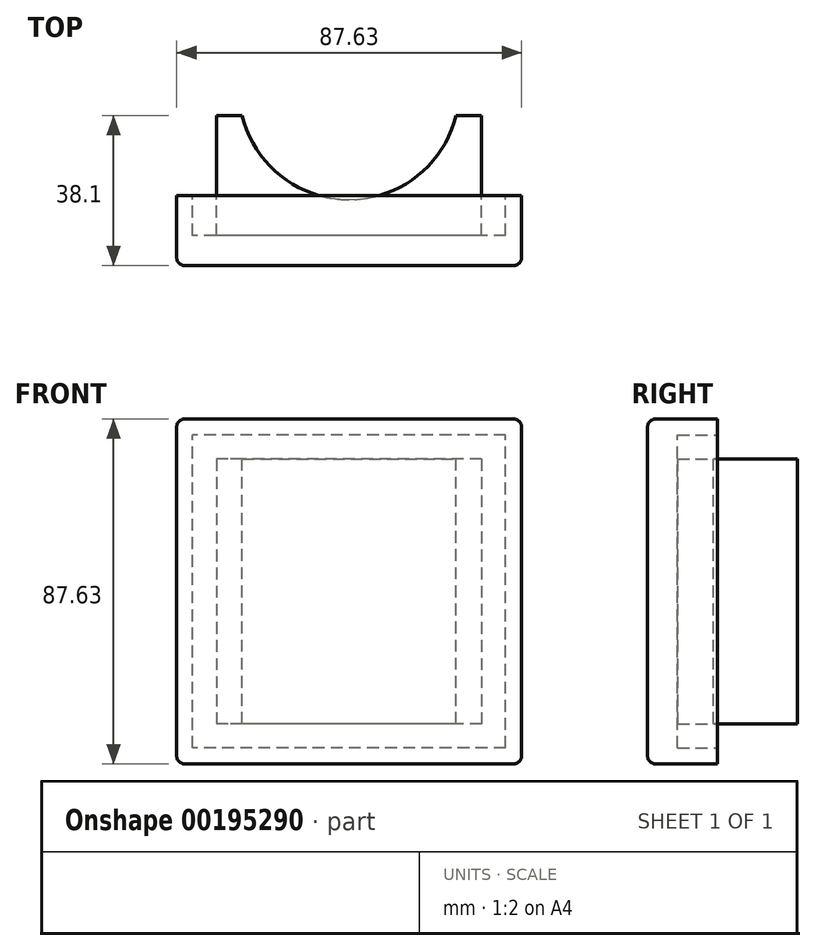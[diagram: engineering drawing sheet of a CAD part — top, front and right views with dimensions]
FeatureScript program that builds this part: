
annotation { "Feature Type Name" : "Feature", "Feature Type Description" : "" }
export const myFeature = defineFeature(function(context is Context, id is Id, definition is map)
    precondition{}
    {
        {
            var Q0;
            Q0=qCreatedBy(makeId("Front.planeOp"),FACE);
            var sketch = newSketch(context, id + "F0", { "sketchPlane" : qUnion([Q0])});
            skLineSegment(sketch, "E0.bottom", {"start": v(-2.03, 0) * mm, "end": v(-85.6, 0) * mm});
            skLineSegment(sketch, "E0.top", {"start": v(-2.03, 87.63) * mm, "end": v(-85.6, 87.63) * mm});
            skLineSegment(sketch, "E0.left", {"start": v(0, 2.03) * mm, "end": v(0, 85.6) * mm});
            skLineSegment(sketch, "E0.right", {"start": v(-87.63, 2.03) * mm, "end": v(-87.63, 85.6) * mm});
            skPoint(sketch, "E1.visualSharp", {"position": v(-87.63, 87.63) * mm});
            skArc(sketch, "E1.filletArc", {"start": v(-85.6, 87.63) * mm, "mid": v(-87.03, 87.03) * mm, "end": v(-87.63, 85.6) * mm});
            skPoint(sketch, "E2.visualSharp", {"position": v(0, 87.63) * mm});
            skArc(sketch, "E2.filletArc", {"start": v(0, 85.6) * mm, "mid": v(-0.6, 87.03) * mm, "end": v(-2.03, 87.63) * mm});
            skPoint(sketch, "E3.visualSharp", {"position": v(0, 0) * mm});
            skArc(sketch, "E3.filletArc", {"start": v(-2.03, 0) * mm, "mid": v(-0.6, 0.6) * mm, "end": v(0, 2.03) * mm});
            skPoint(sketch, "E4.visualSharp", {"position": v(-87.63, 0) * mm});
            skArc(sketch, "E4.filletArc", {"start": v(-87.63, 2.03) * mm, "mid": v(-87.03, 0.6) * mm, "end": v(-85.6, 0) * mm});
            skSolve(sketch);
        }
        {
            var Q0;
            Q0=makeQuery(id+"F0.imprint","IMPRINT",FACE,{"disambiguationData":[TD([[makeQuery(id+"F0.imprint","IMPRINT",EDGE,{"derivedFrom":sQuery(id+"F0.wireOp",EDGE,"E0.bottom")}),-1.0]])]});
            extrude(context, id + "F1", {"entities" : qUnion([Q0]), "depth" : 38.1 * mm});
        }
        {
            var Q0;
            Q0=makeQuery(id+"F1.opExtrude","CAP_FACE",FACE,{"disambiguationData":[OSD([sQuery(id+"F0.wireOp",EDGE,"E0.bottom"),sQuery(id+"F0.wireOp",EDGE,"E0.top"),sQuery(id+"F0.wireOp",EDGE,"E0.left"),sQuery(id+"F0.wireOp",EDGE,"E0.right"),sQuery(id+"F0.wireOp",EDGE,"E1.filletArc"),sQuery(id+"F0.wireOp",EDGE,"E2.filletArc"),sQuery(id+"F0.wireOp",EDGE,"E3.filletArc"),sQuery(id+"F0.wireOp",EDGE,"E4.filletArc")])],"isStart":true});
            var sketch = newSketch(context, id + "F2", { "sketchPlane" : qUnion([Q0])});
            skLineSegment(sketch, "E5.bottom", {"start": v(10.16, 77.47) * mm, "end": v(77.47, 77.47) * mm});
            skLineSegment(sketch, "E5.top", {"start": v(10.16, 10.16) * mm, "end": v(77.47, 10.16) * mm});
            skLineSegment(sketch, "E5.left", {"start": v(10.16, 77.47) * mm, "end": v(10.16, 10.16) * mm});
            skLineSegment(sketch, "E5.right", {"start": v(77.47, 77.47) * mm, "end": v(77.47, 10.16) * mm});
            skLineSegment(sketch, "E6.0", {"start": v(4.06, 83.57) * mm, "end": v(83.57, 83.57) * mm});
            skLineSegment(sketch, "E6.1", {"start": v(4.06, 4.06) * mm, "end": v(4.06, 83.57) * mm});
            skLineSegment(sketch, "E6.2", {"start": v(4.06, 4.06) * mm, "end": v(83.57, 4.06) * mm});
            skLineSegment(sketch, "E6.3", {"start": v(83.57, 4.06) * mm, "end": v(83.57, 83.57) * mm});
            skSolve(sketch);
        }
        {
            var Q0;
            Q0=makeQuery(id+"F2.imprint","IMPRINT",FACE,{"disambiguationData":[TD([[makeQuery(id+"F2.imprint","IMPRINT",EDGE,{"derivedFrom":sQuery(id+"F2.wireOp",EDGE,"E5.bottom")}),1.0]])]});
            extrude(context, id + "F3", {"entities" : qUnion([Q0]), "operationType" : NewBodyOperationType.REMOVE, "oppositeDirection" : true, "depth" : 30.48 * mm});
        }
        {
            var Q0;
            {var subQ0=sQuery(id+"F0.wireOp",EDGE,"E0.bottom");var subQ1=sQuery(id+"F0.wireOp",EDGE,"E4.filletArc");var subQ2=sQuery(id+"F0.wireOp",EDGE,"E3.filletArc");var subQ3=sQuery(id+"F0.wireOp",EDGE,"E2.filletArc");var subQ4=sQuery(id+"F0.wireOp",EDGE,"E1.filletArc");var subQ5=sQuery(id+"F0.wireOp",EDGE,"E0.top");var subQ6=sQuery(id+"F0.wireOp",EDGE,"E0.left");var subQ7=sQuery(id+"F0.wireOp",EDGE,"E0.right");Q0=makeQuery(id+"F3.boolean.opBoolean","SPLIT",FACE,{"disambiguationData":[TD([makeQuery(id+"F1.opExtrude","SWEPT_FACE",FACE,{"disambiguationData":[OSD([subQ0])]})])],"derivedFrom":makeQuery(id+"F1.opExtrude","CAP_FACE",FACE,{"disambiguationData":[OSD([subQ0,subQ5,subQ6,subQ7,subQ4,subQ3,subQ2,subQ1])],"isStart":true})});}
            extrude(context, id + "F4", {"entities" : qUnion([Q0]), "operationType" : NewBodyOperationType.REMOVE, "oppositeDirection" : true, "depth" : 20.32 * mm});
        }
        {
            var Q0;
            Q0=makeQuery(id+"F3.boolean.opBoolean","COPY",FACE,{"derivedFrom":makeQuery(id+"F3.opExtrude","SWEPT_FACE",FACE,{"disambiguationData":[OSD([sQuery(id+"F2.wireOp",EDGE,"E5.bottom")])]})});
            var sketch = newSketch(context, id + "F5", { "sketchPlane" : qUnion([Q0])});
            skCircle(sketch, "E7", {"center": v(-43.82, 6.57) * mm, "radius": 27.94 * mm});
            skSolve(sketch);
        }
        {
            var Q0;
            {var subQ0=sQuery(id+"F5.wireOp",EDGE,"E7");var subQ1=makeQuery(id+"F3.boolean.opBoolean","COPY",EDGE,{"derivedFrom":makeQuery(id+"F3.opExtrude","CAP_EDGE",EDGE,{"disambiguationData":[OSD([sQuery(id+"F2.wireOp",EDGE,"E5.bottom")])],"isStart":true})});var subQ2=makeQuery(id+"F5.imprint","INTERSECT",VERTEX,{"disambiguationData":[OD(0.0)],"derivedFrom":[subQ1,subQ0]});Q0=makeQuery(id+"F5.imprint","IMPRINT",FACE,{"disambiguationData":[TD([[makeQuery(id+"F5.imprint","IMPRINT",EDGE,{"disambiguationData":[TD([[subQ2,1.0]])],"derivedFrom":subQ0}),1.0]])]});}
            extrude(context, id + "F6", {"entities" : qUnion([Q0]), "operationType" : NewBodyOperationType.REMOVE, "endBound" : BoundingType.UP_TO_NEXT, "oppositeDirection" : true, "depth" : 25.4 * mm});
        }
        {
            var Q0;
            Q0=makeQuery(id+"F1.opExtrude","CAP_FACE",FACE,{"disambiguationData":[OSD([sQuery(id+"F0.wireOp",EDGE,"E0.bottom"),sQuery(id+"F0.wireOp",EDGE,"E0.top"),sQuery(id+"F0.wireOp",EDGE,"E0.left"),sQuery(id+"F0.wireOp",EDGE,"E0.right"),sQuery(id+"F0.wireOp",EDGE,"E1.filletArc"),sQuery(id+"F0.wireOp",EDGE,"E2.filletArc"),sQuery(id+"F0.wireOp",EDGE,"E3.filletArc"),sQuery(id+"F0.wireOp",EDGE,"E4.filletArc")])],"isStart":false});
            fillet(context, id + "F7", {"entities" : qUnion([Q0]), "radius" : 2.03 * mm, "tangentPropagation" : true, "allowEdgeOverflow" : false});
        }
    });
